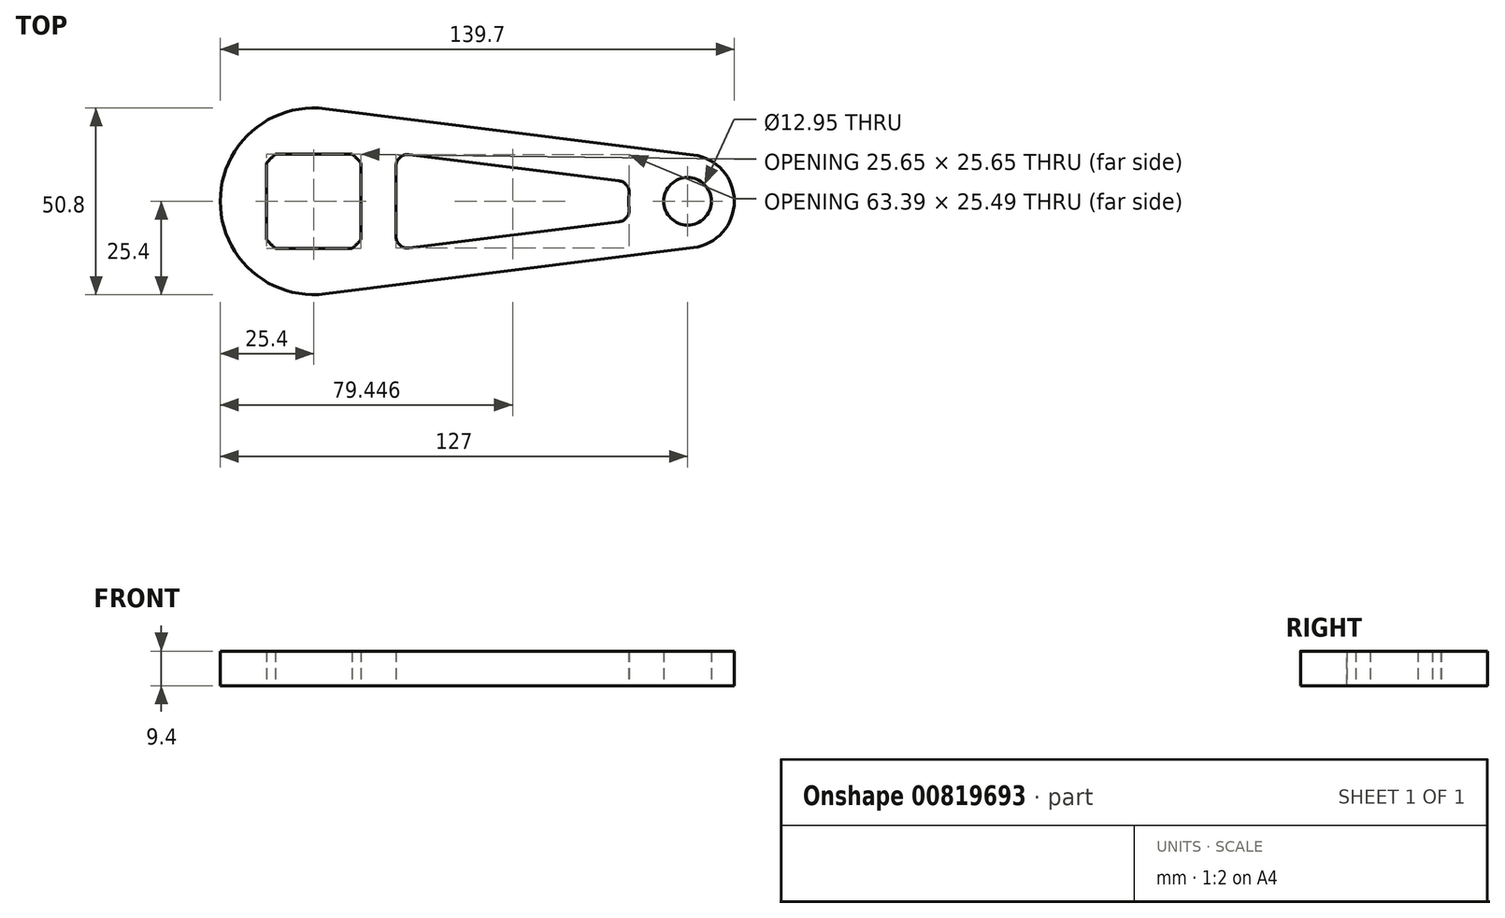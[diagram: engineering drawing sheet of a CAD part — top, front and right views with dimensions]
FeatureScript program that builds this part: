
annotation { "Feature Type Name" : "Feature", "Feature Type Description" : "" }
export const myFeature = defineFeature(function(context is Context, id is Id, definition is map)
    precondition{}
    {
        {
            var Q0;
            Q0=qCreatedBy(makeId("Top.planeOp"),FACE);
            var sketch = newSketch(context, id + "F0", { "sketchPlane" : qUnion([Q0])});
            skLineSegment(sketch, "E0.bottom", {"start": v(10.4, 12.83) * mm, "end": v(-10.4, 12.83) * mm});
            skLineSegment(sketch, "E0.top", {"start": v(10.4, -12.83) * mm, "end": v(-10.4, -12.83) * mm});
            skLineSegment(sketch, "E0.left", {"start": v(12.83, 10.4) * mm, "end": v(12.83, -10.4) * mm});
            skLineSegment(sketch, "E0.right", {"start": v(-12.83, 10.4) * mm, "end": v(-12.83, -10.4) * mm});
            skPoint(sketch, "E0.middle", {"position": v(0, 0) * mm});
            skArc(sketch, "E1", {"start": v(3.17, 25.2) * mm, "mid": v(-25.4, 0) * mm, "end": v(3.17, -25.2) * mm});
            skArc(sketch, "E2", {"start": v(-12.83, -10.4) * mm, "mid": v(-11.67, -11.67) * mm, "end": v(-10.4, -12.83) * mm});
            skPoint(sketch, "E3.orphan", {"position": v(-12.83, 12.83) * mm});
            skArc(sketch, "E4.trimOffspring", {"start": v(-10.4, 12.83) * mm, "mid": v(-11.67, 11.67) * mm, "end": v(-12.83, 10.4) * mm});
            skArc(sketch, "E5.trimOffspring", {"start": v(12.83, 10.4) * mm, "mid": v(11.67, 11.67) * mm, "end": v(10.4, 12.83) * mm});
            skArc(sketch, "E6.trimOffspring", {"start": v(10.4, -12.83) * mm, "mid": v(11.67, -11.67) * mm, "end": v(12.83, -10.4) * mm});
            skPoint(sketch, "E7.orphan", {"position": v(12.83, -12.83) * mm});
            skPoint(sketch, "E8.orphan", {"position": v(12.83, 12.83) * mm});
            skPoint(sketch, "E9.orphan", {"position": v(-12.83, -12.83) * mm});
            skArc(sketch, "E10", {"start": v(103.19, -12.6) * mm, "mid": v(114.3, 0) * mm, "end": v(103.19, 12.6) * mm});
            skLineSegment(sketch, "E11", {"start": v(3.17, 25.2) * mm, "end": v(103.19, 12.6) * mm});
            skLineSegment(sketch, "E12", {"start": v(3.17, -25.2) * mm, "end": v(103.19, -12.6) * mm});
            skCircle(sketch, "E13", {"center": v(101.6, 0) * mm, "radius": 6.48 * mm});
            skLineSegment(sketch, "E14.0", {"start": v(22.35, 13.18) * mm, "end": v(86.44, 5.11) * mm});
            skLineSegment(sketch, "E15.0", {"start": v(22.35, -13.18) * mm, "end": v(86.44, -5.11) * mm});
            skArc(sketch, "E16.0", {"start": v(86.44, 5.11) * mm, "mid": v(85.6, 0) * mm, "end": v(86.44, -5.11) * mm});
            skLineSegment(sketch, "E17.2", {"start": v(22.35, 13.18) * mm, "end": v(22.35, -13.18) * mm});
            skSolve(sketch);
        }
        {
            var Q0;
            Q0=makeQuery(id+"F0.imprint","IMPRINT",FACE,{"disambiguationData":[TD([[makeQuery(id+"F0.imprint","IMPRINT",EDGE,{"derivedFrom":sQuery(id+"F0.wireOp",EDGE,"E0.bottom")}),-1.0]])]});
            extrude(context, id + "F1", {"entities" : qUnion([Q0]), "depth" : 9.4 * mm, "offsetDistance" : 25.4 * mm});
        }
        {
            var Q0;
            Q0=makeQuery(id+"F1.opExtrude","SWEPT_EDGE",EDGE,{"disambiguationData":[OSD([sQuery(id+"F0.wireOp",EDGE,"E14.0"),sQuery(id+"F0.wireOp",EDGE,"E17.2")])]});
            var Q1;
            Q1=makeQuery(id+"F1.opExtrude","SWEPT_EDGE",EDGE,{"disambiguationData":[OSD([sQuery(id+"F0.wireOp",EDGE,"E15.0"),sQuery(id+"F0.wireOp",EDGE,"E17.2")])]});
            var Q2;
            Q2=makeQuery(id+"F1.opExtrude","SWEPT_EDGE",EDGE,{"disambiguationData":[OSD([sQuery(id+"F0.wireOp",EDGE,"E14.0"),sQuery(id+"F0.wireOp",EDGE,"E16.0")])]});
            var Q3;
            Q3=makeQuery(id+"F1.opExtrude","SWEPT_EDGE",EDGE,{"disambiguationData":[OSD([sQuery(id+"F0.wireOp",EDGE,"E15.0"),sQuery(id+"F0.wireOp",EDGE,"E16.0")])]});
            fillet(context, id + "F2", {"entities" : qUnion([Q0, Q1, Q2, Q3]), "radius" : 3.17 * mm, "tangentPropagation" : true, "allowEdgeOverflow" : false});
        }
    });
